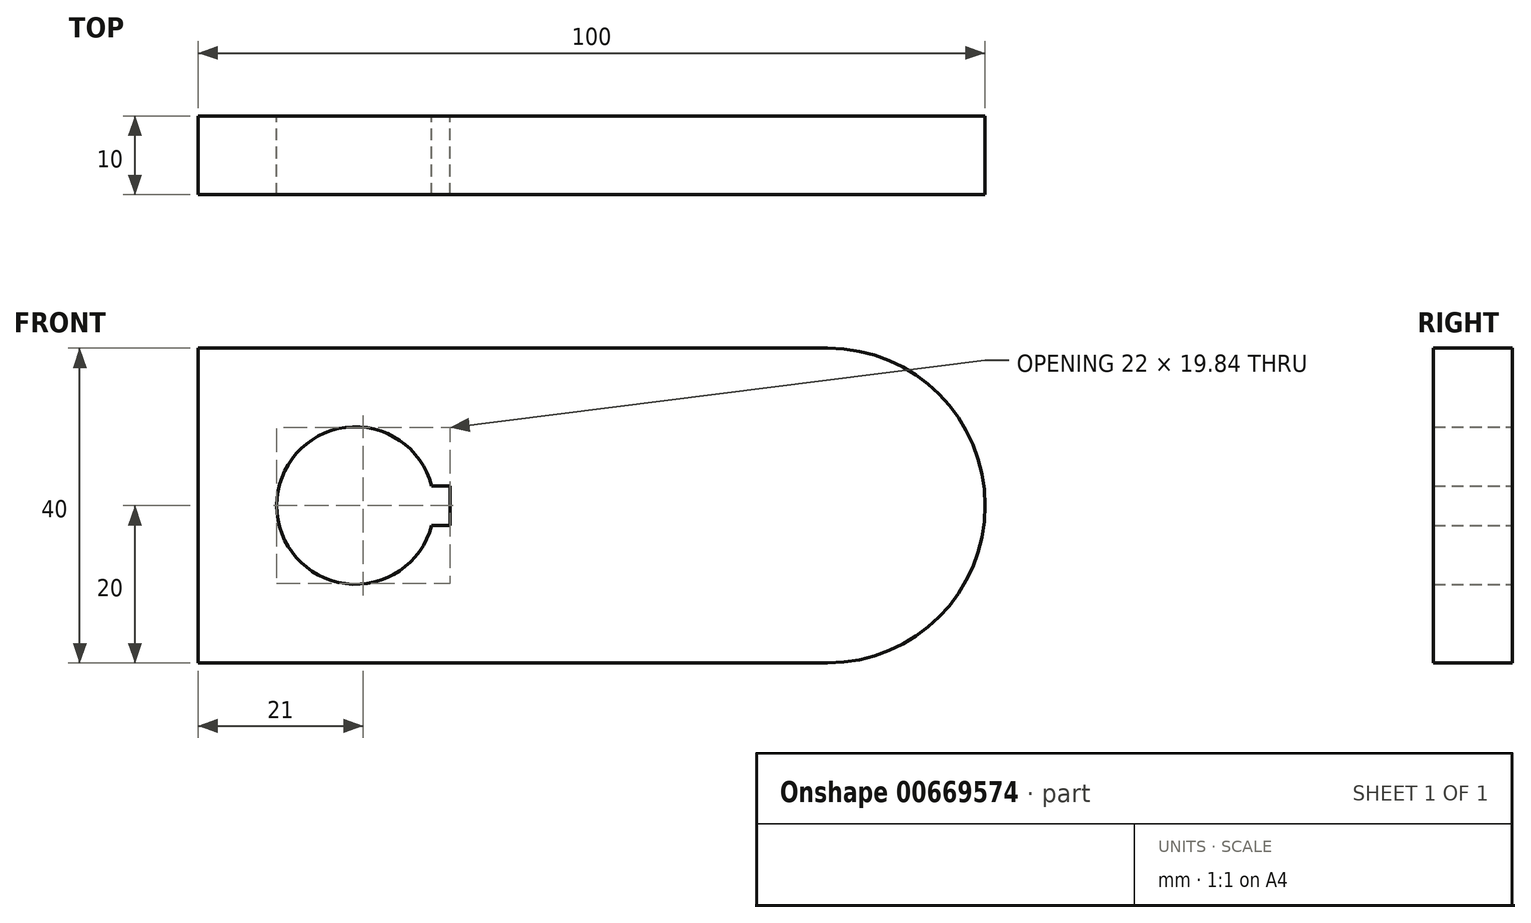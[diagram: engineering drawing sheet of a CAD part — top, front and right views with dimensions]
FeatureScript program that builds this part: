
annotation { "Feature Type Name" : "Feature", "Feature Type Description" : "" }
export const myFeature = defineFeature(function(context is Context, id is Id, definition is map)
    precondition{}
    {
        {
            var Q0;
            Q0=qCreatedBy(makeId("Front.planeOp"),FACE);
            var sketch = newSketch(context, id + "F0", { "sketchPlane" : qUnion([Q0])});
            skCircle(sketch, "E0", {"center": v(0, 0) * mm, "radius": 10 * mm});
            skLineSegment(sketch, "E1", {"start": v(-20, -20) * mm, "end": v(-20, 20) * mm});
            skLineSegment(sketch, "E2", {"start": v(-20, 20) * mm, "end": v(60, 20) * mm});
            skLineSegment(sketch, "E3", {"start": v(80, 0) * mm, "end": v(80, 0) * mm});
            skLineSegment(sketch, "E4", {"start": v(-20, -20) * mm, "end": v(60, -20) * mm});
            skLineSegment(sketch, "E5", {"start": v(0, -2.5) * mm, "end": v(12, -2.5) * mm});
            skLineSegment(sketch, "E6", {"start": v(12, -2.5) * mm, "end": v(12, 2.5) * mm});
            skLineSegment(sketch, "E7", {"start": v(12, 2.5) * mm, "end": v(0, 2.5) * mm});
            skLineSegment(sketch, "E8", {"start": v(0, 2.5) * mm, "end": v(0, -2.5) * mm});
            skPoint(sketch, "E9.visualSharp", {"position": v(80, 20) * mm});
            skArc(sketch, "E9.filletArc", {"start": v(80, 0) * mm, "mid": v(74.14, 14.14) * mm, "end": v(60, 20) * mm});
            skPoint(sketch, "E10.visualSharp", {"position": v(80, -20) * mm});
            skArc(sketch, "E10.filletArc", {"start": v(60, -20) * mm, "mid": v(74.14, -14.14) * mm, "end": v(80, 0) * mm});
            skSolve(sketch);
        }
        {
            var Q0;
            Q0=makeQuery(id+"F0.imprint","IMPRINT",FACE,{"disambiguationData":[TD([[makeQuery(id+"F0.imprint","IMPRINT",EDGE,{"derivedFrom":sQuery(id+"F0.wireOp",EDGE,"E1")}),-1.0]])]});
            extrude(context, id + "F1", {"entities" : qUnion([Q0]), "depth" : 10 * mm, "offsetDistance" : 25 * mm});
        }
    });
